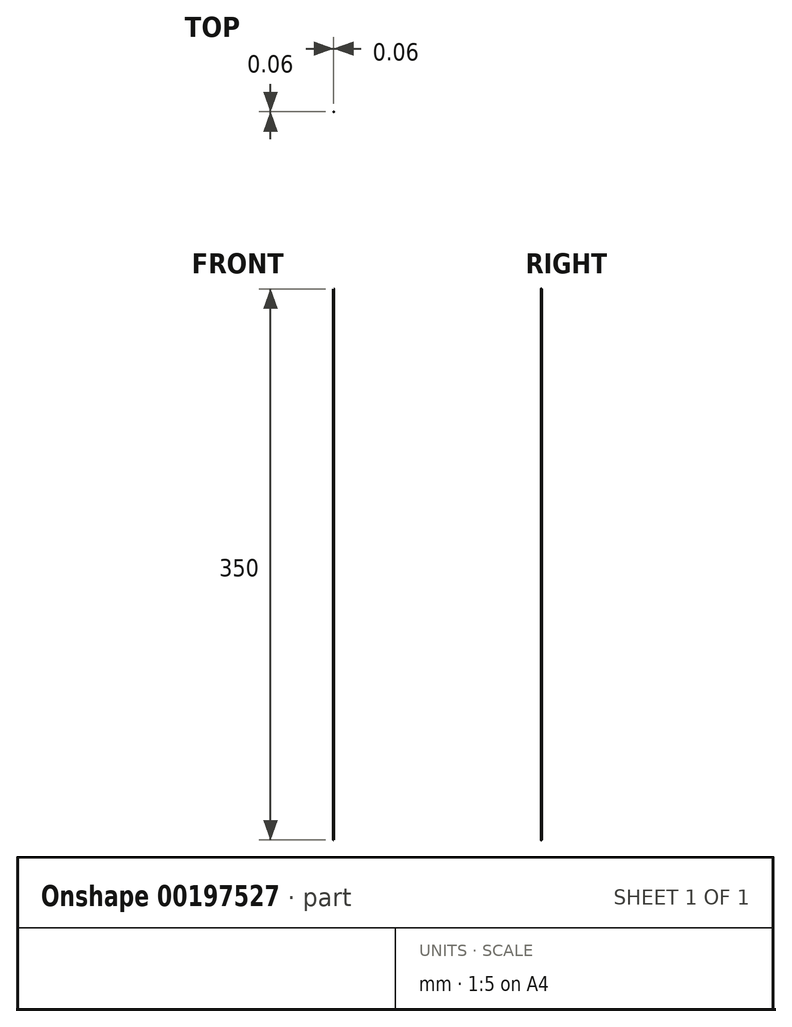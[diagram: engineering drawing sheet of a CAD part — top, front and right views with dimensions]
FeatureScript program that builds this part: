
annotation { "Feature Type Name" : "Feature", "Feature Type Description" : "" }
export const myFeature = defineFeature(function(context is Context, id is Id, definition is map)
    precondition{}
    {
        {
            var Q0;
            Q0=qCreatedBy(makeId("Top.planeOp"),FACE);
            var sketch = newSketch(context, id + "F0", { "sketchPlane" : qUnion([Q0])});
            skCircle(sketch, "E0", {"center": v(0, 0) * mm, "radius": 0.03 * mm});
            skSolve(sketch);
        }
        {
            var Q0;
            Q0=qSketchRegion(id+"F0",true);
            extrude(context, id + "F1", {"entities" : qUnion([Q0]), "depth" : 350 * mm});
        }
    });
